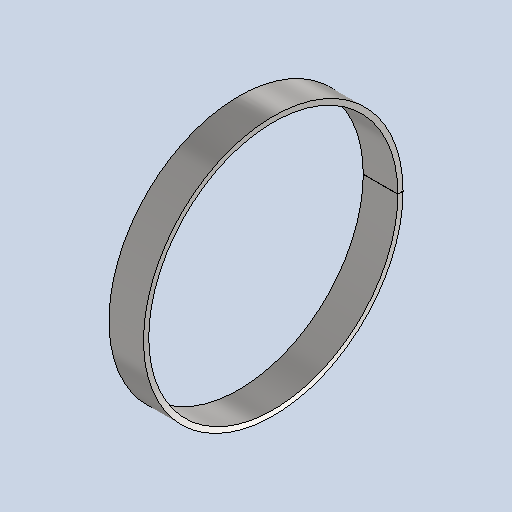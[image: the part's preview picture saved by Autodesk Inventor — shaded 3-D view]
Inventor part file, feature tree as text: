
AUTODESK INVENTOR PART (.ipt)
format: ipt  version: 2025 (Build 290162010, 162A)  size: 150,016 bytes
history: native  units: mm
features: revolve x1, sketch x1, other x1
ambient origin geometry x8: Origin, YZ Plane, XZ Plane, XY Plane, X Axis, Y Axis, Z Axis, Center Point
bodies: Solid1 (feature_tree)
feature tree (3):
  revolve  "Revolution1"  [1 undecoded]
  sketch  "Sketch1"  dims[d2=3.0mm d3=20.0mm d4=75.0mm d5=62.8144mm]
  other  "Definition1"
note: 1 required parameter value undecoded (feature->parameter linkage not recoverable at this tier; creation-order binding heuristic only, values carry confidence <= 0.55)
